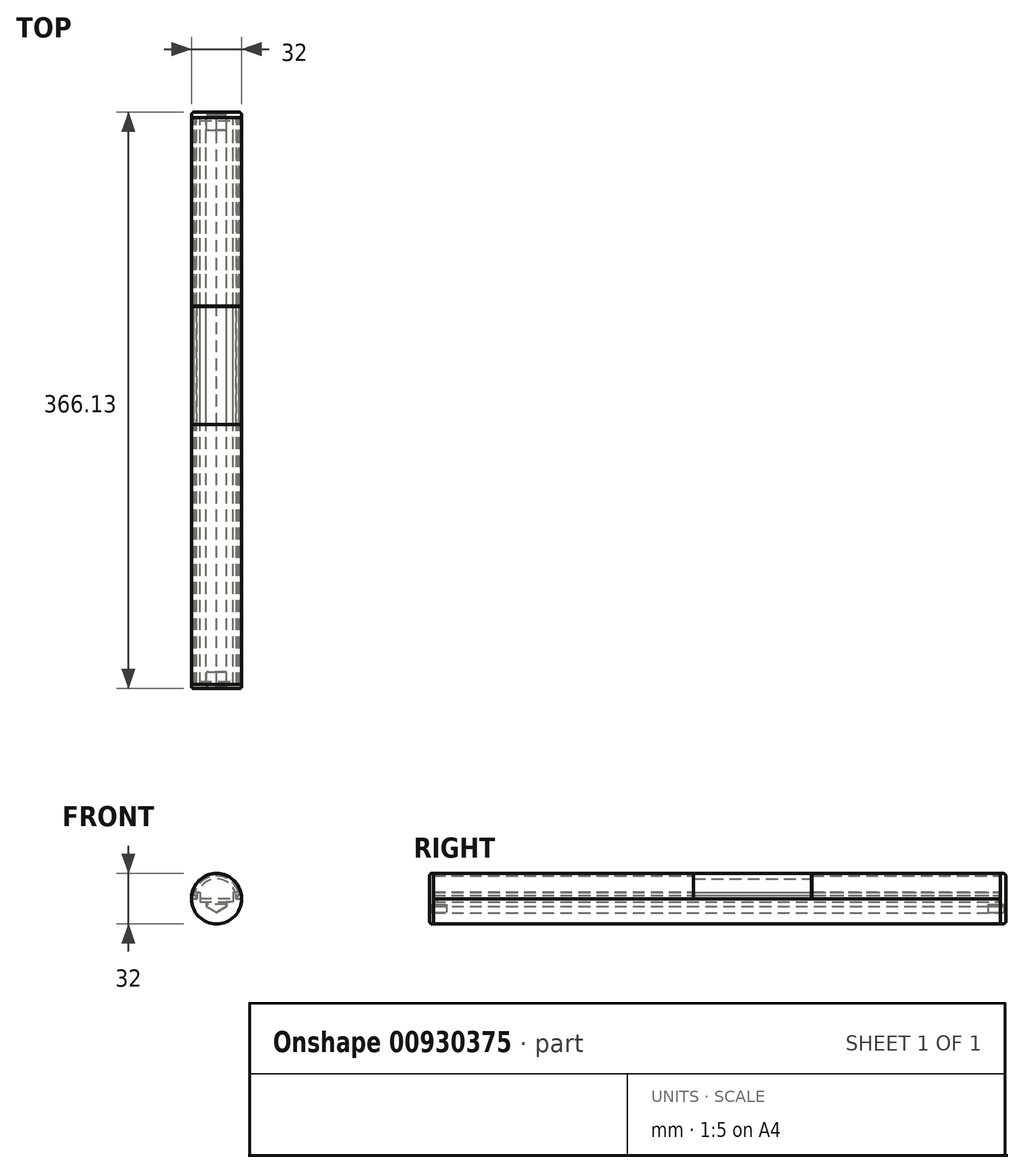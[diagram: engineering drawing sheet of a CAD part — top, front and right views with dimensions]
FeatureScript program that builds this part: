
annotation { "Feature Type Name" : "Feature", "Feature Type Description" : "" }
export const myFeature = defineFeature(function(context is Context, id is Id, definition is map)
    precondition{}
    {
        {
            var Q0;
            Q0=qCreatedBy(makeId("Front.planeOp"),FACE);
            var sketch = newSketch(context, id + "F0", { "sketchPlane" : qUnion([Q0])});
            skArc(sketch, "E0", {"start": v(0, -16) * mm, "mid": v(11.31, -11.31) * mm, "end": v(16, 0) * mm});
            skLineSegment(sketch, "E1", {"start": v(16, 0) * mm, "end": v(12.75, 0) * mm});
            skLineSegment(sketch, "E2", {"start": v(12.75, 0) * mm, "end": v(12.75, 2.1) * mm});
            skLineSegment(sketch, "E3", {"start": v(12.75, 2.1) * mm, "end": v(14.25, 2.1) * mm});
            skLineSegment(sketch, "E4", {"start": v(14.25, 2.1) * mm, "end": v(14.25, 4.1) * mm});
            skLineSegment(sketch, "E5", {"start": v(14.25, 4.1) * mm, "end": v(10.5, 4.1) * mm});
            skLineSegment(sketch, "E6", {"start": v(10.5, 4.1) * mm, "end": v(10.5, -1.9) * mm});
            skLineSegment(sketch, "E7", {"start": v(10.5, -1.9) * mm, "end": v(6.5, -1.9) * mm});
            skLineSegment(sketch, "E8", {"start": v(6.5, -1.9) * mm, "end": v(6.5, -4.9) * mm});
            skLineSegment(sketch, "E9", {"start": v(6.5, -4.9) * mm, "end": v(0, -8.88) * mm});
            skLineSegment(sketch, "E10", {"start": v(0, -8.88) * mm, "end": v(0, -16) * mm});
            skLineSegment(sketch, "E11.MirrorCS", {"start": v(-14.25, 2.1) * mm, "end": v(-14.25, 4.1) * mm});
            skLineSegment(sketch, "E12.MirrorCS", {"start": v(-12.75, 0) * mm, "end": v(-12.75, 2.1) * mm});
            skLineSegment(sketch, "E13.MirrorCS", {"start": v(-12.75, 2.1) * mm, "end": v(-14.25, 2.1) * mm});
            skLineSegment(sketch, "E14.MirrorCS", {"start": v(-6.5, -1.9) * mm, "end": v(-6.5, -4.9) * mm});
            skLineSegment(sketch, "E15.MirrorCS", {"start": v(-10.5, 4.1) * mm, "end": v(-10.5, -1.9) * mm});
            skLineSegment(sketch, "E16.MirrorCS", {"start": v(-6.5, -4.9) * mm, "end": v(0, -8.88) * mm});
            skLineSegment(sketch, "E17.MirrorCS", {"start": v(-14.25, 4.1) * mm, "end": v(-10.5, 4.1) * mm});
            skArc(sketch, "E18.MirrorCS", {"start": v(0, -16) * mm, "mid": v(-11.31, -11.31) * mm, "end": v(-16, 0) * mm});
            skLineSegment(sketch, "E19.MirrorCS", {"start": v(-10.5, -1.9) * mm, "end": v(-6.5, -1.9) * mm});
            skLineSegment(sketch, "E20.MirrorCS", {"start": v(-16, 0) * mm, "end": v(-12.75, 0) * mm});
            skSolve(sketch);
        }
        {
            var Q0;
            Q0=makeQuery(id+"F0.imprint","IMPRINT",FACE,{"disambiguationData":[TD([[makeQuery(id+"F0.imprint","IMPRINT",EDGE,{"derivedFrom":sQuery(id+"F0.wireOp",EDGE,"E0")}),1.0]])]});
            var Q1;
            Q1=makeQuery(id+"F0.imprint","IMPRINT",FACE,{"disambiguationData":[TD([[makeQuery(id+"F0.imprint","IMPRINT",EDGE,{"derivedFrom":sQuery(id+"F0.wireOp",EDGE,"E10")}),-1.0]])]});
            extrude(context, id + "F1", {"entities" : qUnion([Q0, Q1]), "endBound" : BoundingType.SYMMETRIC, "depth" : 360 * mm, "offsetDistance" : 25 * mm});
        }
        {
            var Q0;
            Q0=qCreatedBy(makeId("Front.planeOp"),FACE);
            var sketch = newSketch(context, id + "F2", { "sketchPlane" : qUnion([Q0])});
            skArc(sketch, "E21", {"start": v(16, 6.65) * mm, "mid": v(11.31, 17.96) * mm, "end": v(0, 22.65) * mm});
            skArc(sketch, "E22", {"start": v(0, 21.15) * mm, "mid": v(8.62, 18.3) * mm, "end": v(13.86, 10.9) * mm});
            skLineSegment(sketch, "E23", {"start": v(13.86, 10.9) * mm, "end": v(14.46, 10.9) * mm});
            skLineSegment(sketch, "E24", {"start": v(14.46, 10.9) * mm, "end": v(14.46, 8.65) * mm});
            skLineSegment(sketch, "E25", {"start": v(14.46, 8.65) * mm, "end": v(12.93, 8.65) * mm});
            skLineSegment(sketch, "E26", {"start": v(12.93, 8.65) * mm, "end": v(12.93, 6.65) * mm});
            skLineSegment(sketch, "E27", {"start": v(12.93, 6.65) * mm, "end": v(16, 6.65) * mm});
            skLineSegment(sketch, "E28", {"start": v(0, 22.65) * mm, "end": v(0, 21.15) * mm});
            skArc(sketch, "E29.MirrorCS", {"start": v(0, 21.15) * mm, "mid": v(-8.62, 18.3) * mm, "end": v(-13.86, 10.9) * mm});
            skArc(sketch, "E30.MirrorCS", {"start": v(-16, 6.65) * mm, "mid": v(-11.31, 17.96) * mm, "end": v(0, 22.65) * mm});
            skLineSegment(sketch, "E31.MirrorCS", {"start": v(-13.86, 10.9) * mm, "end": v(-14.46, 10.9) * mm});
            skLineSegment(sketch, "E32.MirrorCS", {"start": v(-14.46, 10.9) * mm, "end": v(-14.46, 8.65) * mm});
            skLineSegment(sketch, "E33.MirrorCS", {"start": v(-14.46, 8.65) * mm, "end": v(-12.93, 8.65) * mm});
            skLineSegment(sketch, "E34.MirrorCS", {"start": v(-12.93, 8.65) * mm, "end": v(-12.93, 6.65) * mm});
            skLineSegment(sketch, "E35.MirrorCS", {"start": v(-12.93, 6.65) * mm, "end": v(-16, 6.65) * mm});
            skSolve(sketch);
        }
        {
            var Q0;
            Q0 = qSketchRegion(id + "F2", true);
            extrude(context, id + "F3", {"entities" : qUnion([Q0]), "depth" : 120 * mm, "offsetDistance" : 25 * mm});
        }
        {
            var Q0;
            Q0=qCreatedBy(makeId("Front.planeOp"),FACE);
            var sketch = newSketch(context, id + "F4", { "sketchPlane" : qUnion([Q0])});
            skCircle(sketch, "E36", {"center": v(33.5, 0) * mm, "radius": 16 * mm});
            skSolve(sketch);
        }
        {
            var Q0;
            Q0=makeQuery(id+"F4.imprint","IMPRINT",FACE,{"disambiguationData":[TD([[makeQuery(id+"F4.imprint","IMPRINT",EDGE,{"derivedFrom":sQuery(id+"F4.wireOp",EDGE,"E36")}),1.0]])]});
            extrude(context, id + "F5", {"entities" : qUnion([Q0]), "depth" : 3.5 * mm, "offsetDistance" : 25 * mm});
        }
        {
            var Q0;
            Q0=makeQuery(id+"F3.opExtrude","SWEPT_BODY",BODY,{"disambiguationData":[OSD([sQuery(id+"F2.wireOp",EDGE,"E21"),sQuery(id+"F2.wireOp",EDGE,"E22"),sQuery(id+"F2.wireOp",EDGE,"E23"),sQuery(id+"F2.wireOp",EDGE,"E24"),sQuery(id+"F2.wireOp",EDGE,"E25"),sQuery(id+"F2.wireOp",EDGE,"E26"),sQuery(id+"F2.wireOp",EDGE,"E27"),sQuery(id+"F2.wireOp",EDGE,"E29.MirrorCS"),sQuery(id+"F2.wireOp",EDGE,"E30.MirrorCS"),sQuery(id+"F2.wireOp",EDGE,"E31.MirrorCS"),sQuery(id+"F2.wireOp",EDGE,"E32.MirrorCS"),sQuery(id+"F2.wireOp",EDGE,"E33.MirrorCS"),sQuery(id+"F2.wireOp",EDGE,"E34.MirrorCS"),sQuery(id+"F2.wireOp",EDGE,"E35.MirrorCS")])]});
            transform(context, id + "F6", {"entities" : qUnion([Q0]), "transformType" : TransformType.TRANSLATION_3D, "dx" : 0 * mm, "dy" : 155 * mm, "dz" : 0 * mm, "makeCopy" : true});
        }
        {
            var Q0;
            Q0=makeQuery(id+"F5.opExtrude","SWEPT_BODY",BODY,{"disambiguationData":[OSD([sQuery(id+"F4.wireOp",EDGE,"E36")])]});
            transform(context, id + "F7", {"entities" : qUnion([Q0]), "transformType" : TransformType.TRANSLATION_3D, "dx" : -33.5 * mm, "dy" : 184.33 * mm, "dz" : 0 * mm, "makeCopy" : false});
        }
        {
            var Q0;
            Q0=makeQuery(id+"F5.opExtrude","CAP_EDGE",EDGE,{"disambiguationData":[OSD([sQuery(id+"F4.wireOp",EDGE,"E36")])],"isStart":true});
            fillet(context, id + "F8", {"entities" : qUnion([Q0]), "radius" : 2 * mm, "tangentPropagation" : true, "allowEdgeOverflow" : false});
        }
        {
            var Q0;
            Q0=makeQuery(id+"F5.opExtrude","SWEPT_BODY",BODY,{"disambiguationData":[OSD([sQuery(id+"F4.wireOp",EDGE,"E36")])]});
            transform(context, id + "F9", {"entities" : qUnion([Q0]), "transformType" : TransformType.TRANSLATION_3D, "dx" : 0 * mm, "dy" : -0.8 * mm, "dz" : 0 * mm, "makeCopy" : false});
        }
        {
            var Q0;
            Q0=qCreatedBy(makeId("Front.planeOp"),FACE);
            var sketch = newSketch(context, id + "F10", { "sketchPlane" : qUnion([Q0])});
            skCircle(sketch, "E37", {"center": v(33.5, 0) * mm, "radius": 16 * mm});
            skSolve(sketch);
        }
        {
            var Q0;
            Q0=makeQuery(id+"F10.imprint","IMPRINT",FACE,{"disambiguationData":[TD([[makeQuery(id+"F10.imprint","IMPRINT",EDGE,{"derivedFrom":sQuery(id+"F10.wireOp",EDGE,"E37")}),1.0]])]});
            extrude(context, id + "F11", {"entities" : qUnion([Q0]), "depth" : 2.5 * mm, "offsetDistance" : 25 * mm});
        }
        {
            var Q0;
            Q0=makeQuery(id+"F11.opExtrude","SWEPT_BODY",BODY,{"disambiguationData":[OSD([sQuery(id+"F10.wireOp",EDGE,"E37")])]});
            transform(context, id + "F12", {"entities" : qUnion([Q0]), "transformType" : TransformType.TRANSLATION_3D, "dx" : 0 * mm, "dy" : -180 * mm, "dz" : 0 * mm, "makeCopy" : false});
        }
        {
            var Q0;
            Q0=makeQuery(id+"F3.opExtrude","SWEPT_BODY",BODY,{"disambiguationData":[OSD([sQuery(id+"F2.wireOp",EDGE,"E21"),sQuery(id+"F2.wireOp",EDGE,"E22"),sQuery(id+"F2.wireOp",EDGE,"E23"),sQuery(id+"F2.wireOp",EDGE,"E24"),sQuery(id+"F2.wireOp",EDGE,"E25"),sQuery(id+"F2.wireOp",EDGE,"E26"),sQuery(id+"F2.wireOp",EDGE,"E27"),sQuery(id+"F2.wireOp",EDGE,"E29.MirrorCS"),sQuery(id+"F2.wireOp",EDGE,"E30.MirrorCS"),sQuery(id+"F2.wireOp",EDGE,"E31.MirrorCS"),sQuery(id+"F2.wireOp",EDGE,"E32.MirrorCS"),sQuery(id+"F2.wireOp",EDGE,"E33.MirrorCS"),sQuery(id+"F2.wireOp",EDGE,"E34.MirrorCS"),sQuery(id+"F2.wireOp",EDGE,"E35.MirrorCS")])]});
            transform(context, id + "F13", {"entities" : qUnion([Q0]), "transformType" : TransformType.TRANSLATION_3D, "dx" : 0 * mm, "dy" : -30 * mm, "dz" : -6.7 * mm, "makeCopy" : false});
        }
        {
            var Q0;
            Q0=makeQuery(id+"F11.opExtrude","SWEPT_BODY",BODY,{"disambiguationData":[OSD([sQuery(id+"F10.wireOp",EDGE,"E37")])]});
            transform(context, id + "F14", {"entities" : qUnion([Q0]), "transformType" : TransformType.TRANSLATION_3D, "dx" : -33.5 * mm, "dy" : 0 * mm, "dz" : 0 * mm, "makeCopy" : false});
        }
        {
            var Q0;
            Q0=makeQuery(id+"F11.opExtrude","CAP_EDGE",EDGE,{"disambiguationData":[OSD([sQuery(id+"F10.wireOp",EDGE,"E37")])],"isStart":false});
            fillet(context, id + "F15", {"entities" : qUnion([Q0]), "radius" : 1.5 * mm, "tangentPropagation" : true, "allowEdgeOverflow" : false});
        }
        {
            var Q0;
            Q0=makeQuery(id+"F3.opExtrude","SWEPT_BODY",BODY,{"disambiguationData":[OSD([sQuery(id+"F2.wireOp",EDGE,"E21"),sQuery(id+"F2.wireOp",EDGE,"E22"),sQuery(id+"F2.wireOp",EDGE,"E23"),sQuery(id+"F2.wireOp",EDGE,"E24"),sQuery(id+"F2.wireOp",EDGE,"E25"),sQuery(id+"F2.wireOp",EDGE,"E26"),sQuery(id+"F2.wireOp",EDGE,"E27"),sQuery(id+"F2.wireOp",EDGE,"E29.MirrorCS"),sQuery(id+"F2.wireOp",EDGE,"E30.MirrorCS"),sQuery(id+"F2.wireOp",EDGE,"E31.MirrorCS"),sQuery(id+"F2.wireOp",EDGE,"E32.MirrorCS"),sQuery(id+"F2.wireOp",EDGE,"E33.MirrorCS"),sQuery(id+"F2.wireOp",EDGE,"E34.MirrorCS"),sQuery(id+"F2.wireOp",EDGE,"E35.MirrorCS")])]});
            transform(context, id + "F16", {"entities" : qUnion([Q0]), "transformType" : TransformType.TRANSLATION_3D, "dx" : 0 * mm, "dy" : 210.3 * mm, "dz" : 0 * mm, "makeCopy" : true});
        }
        {
            var Q0;
            Q0=makeQuery(id+"F6.opPattern","COPY",BODY,{"derivedFrom":makeQuery(id+"F3.opExtrude","SWEPT_BODY",BODY,{"disambiguationData":[OSD([sQuery(id+"F2.wireOp",EDGE,"E21"),sQuery(id+"F2.wireOp",EDGE,"E22"),sQuery(id+"F2.wireOp",EDGE,"E23"),sQuery(id+"F2.wireOp",EDGE,"E24"),sQuery(id+"F2.wireOp",EDGE,"E25"),sQuery(id+"F2.wireOp",EDGE,"E26"),sQuery(id+"F2.wireOp",EDGE,"E27"),sQuery(id+"F2.wireOp",EDGE,"E29.MirrorCS"),sQuery(id+"F2.wireOp",EDGE,"E30.MirrorCS"),sQuery(id+"F2.wireOp",EDGE,"E31.MirrorCS"),sQuery(id+"F2.wireOp",EDGE,"E32.MirrorCS"),sQuery(id+"F2.wireOp",EDGE,"E33.MirrorCS"),sQuery(id+"F2.wireOp",EDGE,"E34.MirrorCS"),sQuery(id+"F2.wireOp",EDGE,"E35.MirrorCS")])]}),"instanceName":"1"});
            deleteBodies(context, id + "F17", {"entities" : qUnion([Q0])});
        }
        {
            var Q0;
            Q0=qCreatedBy(makeId("Front.planeOp"),FACE);
            var sketch = newSketch(context, id + "F18", { "sketchPlane" : qUnion([Q0])});
            skArc(sketch, "E38", {"start": v(0, 44) * mm, "mid": v(11.31, 39.31) * mm, "end": v(16, 28) * mm});
            skArc(sketch, "E39", {"start": v(0, 42.5) * mm, "mid": v(8.64, 39.64) * mm, "end": v(13.88, 32.2) * mm});
            skLineSegment(sketch, "E40", {"start": v(13.88, 32.2) * mm, "end": v(14.48, 32.2) * mm});
            skLineSegment(sketch, "E41", {"start": v(14.48, 32.2) * mm, "end": v(14.49, 29.95) * mm});
            skLineSegment(sketch, "E42", {"start": v(14.49, 29.95) * mm, "end": v(12.99, 29.95) * mm});
            skLineSegment(sketch, "E43", {"start": v(12.99, 29.95) * mm, "end": v(13, 27.95) * mm});
            skLineSegment(sketch, "E44", {"start": v(13, 27.95) * mm, "end": v(16, 28) * mm});
            skLineSegment(sketch, "E45", {"start": v(0, 44) * mm, "end": v(0, 42.5) * mm});
            skArc(sketch, "E46.MirrorCS", {"start": v(0, 44) * mm, "mid": v(-11.31, 39.31) * mm, "end": v(-16, 28) * mm});
            skArc(sketch, "E47.MirrorCS", {"start": v(0, 42.5) * mm, "mid": v(-8.64, 39.64) * mm, "end": v(-13.88, 32.2) * mm});
            skLineSegment(sketch, "E48.MirrorCS", {"start": v(-13.88, 32.2) * mm, "end": v(-14.48, 32.2) * mm});
            skLineSegment(sketch, "E49.MirrorCS", {"start": v(-14.48, 32.2) * mm, "end": v(-14.49, 29.95) * mm});
            skLineSegment(sketch, "E50.MirrorCS", {"start": v(-14.49, 29.95) * mm, "end": v(-12.99, 29.95) * mm});
            skLineSegment(sketch, "E51.MirrorCS", {"start": v(-12.99, 29.95) * mm, "end": v(-13, 27.95) * mm});
            skLineSegment(sketch, "E52.MirrorCS", {"start": v(-13, 27.95) * mm, "end": v(-16, 28) * mm});
            skSolve(sketch);
        }
        {
            var Q0;
            Q0 = qSketchRegion(id + "F18", true);
            extrude(context, id + "F19", {"entities" : qUnion([Q0]), "endBound" : BoundingType.SYMMETRIC, "depth" : 165 * mm, "offsetDistance" : 25 * mm});
        }
        {
            var Q0;
            Q0=makeQuery(id+"F19.opExtrude","SWEPT_BODY",BODY,{"disambiguationData":[OSD([sQuery(id+"F18.wireOp",EDGE,"E38"),sQuery(id+"F18.wireOp",EDGE,"E39"),sQuery(id+"F18.wireOp",EDGE,"E40"),sQuery(id+"F18.wireOp",EDGE,"E41"),sQuery(id+"F18.wireOp",EDGE,"E42"),sQuery(id+"F18.wireOp",EDGE,"E43"),sQuery(id+"F18.wireOp",EDGE,"E44"),sQuery(id+"F18.wireOp",EDGE,"E46.MirrorCS"),sQuery(id+"F18.wireOp",EDGE,"E47.MirrorCS"),sQuery(id+"F18.wireOp",EDGE,"E48.MirrorCS"),sQuery(id+"F18.wireOp",EDGE,"E49.MirrorCS"),sQuery(id+"F18.wireOp",EDGE,"E50.MirrorCS"),sQuery(id+"F18.wireOp",EDGE,"E51.MirrorCS"),sQuery(id+"F18.wireOp",EDGE,"E52.MirrorCS")])]});
            transform(context, id + "F20", {"entities" : qUnion([Q0]), "transformType" : TransformType.TRANSLATION_3D, "dx" : 0 * mm, "dy" : 90 * mm, "dz" : -28 * mm, "makeCopy" : false});
        }
        {
            var Q0;
            Q0=makeQuery(id+"F3.opExtrude","SWEPT_BODY",BODY,{"disambiguationData":[OSD([sQuery(id+"F2.wireOp",EDGE,"E21"),sQuery(id+"F2.wireOp",EDGE,"E22"),sQuery(id+"F2.wireOp",EDGE,"E23"),sQuery(id+"F2.wireOp",EDGE,"E24"),sQuery(id+"F2.wireOp",EDGE,"E25"),sQuery(id+"F2.wireOp",EDGE,"E26"),sQuery(id+"F2.wireOp",EDGE,"E27"),sQuery(id+"F2.wireOp",EDGE,"E29.MirrorCS"),sQuery(id+"F2.wireOp",EDGE,"E30.MirrorCS"),sQuery(id+"F2.wireOp",EDGE,"E31.MirrorCS"),sQuery(id+"F2.wireOp",EDGE,"E32.MirrorCS"),sQuery(id+"F2.wireOp",EDGE,"E33.MirrorCS"),sQuery(id+"F2.wireOp",EDGE,"E34.MirrorCS"),sQuery(id+"F2.wireOp",EDGE,"E35.MirrorCS")])]});
            deleteBodies(context, id + "F21", {"entities" : qUnion([Q0])});
        }
        {
            var Q0;
            Q0=makeQuery(id+"F19.opExtrude","SWEPT_BODY",BODY,{"disambiguationData":[OSD([sQuery(id+"F18.wireOp",EDGE,"E38"),sQuery(id+"F18.wireOp",EDGE,"E39"),sQuery(id+"F18.wireOp",EDGE,"E40"),sQuery(id+"F18.wireOp",EDGE,"E41"),sQuery(id+"F18.wireOp",EDGE,"E42"),sQuery(id+"F18.wireOp",EDGE,"E43"),sQuery(id+"F18.wireOp",EDGE,"E44"),sQuery(id+"F18.wireOp",EDGE,"E46.MirrorCS"),sQuery(id+"F18.wireOp",EDGE,"E47.MirrorCS"),sQuery(id+"F18.wireOp",EDGE,"E48.MirrorCS"),sQuery(id+"F18.wireOp",EDGE,"E49.MirrorCS"),sQuery(id+"F18.wireOp",EDGE,"E50.MirrorCS"),sQuery(id+"F18.wireOp",EDGE,"E51.MirrorCS"),sQuery(id+"F18.wireOp",EDGE,"E52.MirrorCS")])]});
            transform(context, id + "F22", {"entities" : qUnion([Q0]), "transformType" : TransformType.TRANSLATION_3D, "dx" : 0 * mm, "dy" : -149.5 * mm, "dz" : 0 * mm, "makeCopy" : false});
        }
        {
            var Q0;
            Q0=makeQuery(id+"F11.opExtrude","SWEPT_BODY",BODY,{"disambiguationData":[OSD([sQuery(id+"F10.wireOp",EDGE,"E37")])]});
            transform(context, id + "F23", {"entities" : qUnion([Q0]), "transformType" : TransformType.TRANSLATION_3D, "dx" : 0 * mm, "dy" : -45.1 * mm, "dz" : 0 * mm, "makeCopy" : false});
        }
        {
            var Q0;
            Q0=makeQuery(id+"F19.opExtrude","SWEPT_BODY",BODY,{"disambiguationData":[OSD([sQuery(id+"F18.wireOp",EDGE,"E38"),sQuery(id+"F18.wireOp",EDGE,"E39"),sQuery(id+"F18.wireOp",EDGE,"E40"),sQuery(id+"F18.wireOp",EDGE,"E41"),sQuery(id+"F18.wireOp",EDGE,"E42"),sQuery(id+"F18.wireOp",EDGE,"E43"),sQuery(id+"F18.wireOp",EDGE,"E44"),sQuery(id+"F18.wireOp",EDGE,"E46.MirrorCS"),sQuery(id+"F18.wireOp",EDGE,"E47.MirrorCS"),sQuery(id+"F18.wireOp",EDGE,"E48.MirrorCS"),sQuery(id+"F18.wireOp",EDGE,"E49.MirrorCS"),sQuery(id+"F18.wireOp",EDGE,"E50.MirrorCS"),sQuery(id+"F18.wireOp",EDGE,"E51.MirrorCS"),sQuery(id+"F18.wireOp",EDGE,"E52.MirrorCS")])]});
            transform(context, id + "F24", {"entities" : qUnion([Q0]), "transformType" : TransformType.TRANSLATION_3D, "dx" : 0 * mm, "dy" : -45.55 * mm, "dz" : 0 * mm, "makeCopy" : false});
        }
        {
            var Q0;
            Q0=qCreatedBy(makeId("Front.planeOp"),FACE);
            var sketch = newSketch(context, id + "F25", { "sketchPlane" : qUnion([Q0])});
            skLineSegment(sketch, "E53", {"start": v(-6.4, -4.8) * mm, "end": v(0, -8.7) * mm});
            skLineSegment(sketch, "E54", {"start": v(0, -8.7) * mm, "end": v(6.4, -4.8) * mm});
            skLineSegment(sketch, "E55", {"start": v(6.4, -4.8) * mm, "end": v(6.4, -3.55) * mm});
            skLineSegment(sketch, "E56", {"start": v(6.4, -3.55) * mm, "end": v(-6.4, -3.55) * mm});
            skLineSegment(sketch, "E57", {"start": v(-6.4, -3.55) * mm, "end": v(-6.4, -4.8) * mm});
            skSolve(sketch);
        }
        {
            var Q0;
            Q0=makeQuery(id+"F25.imprint","IMPRINT",FACE,{"disambiguationData":[TD([[makeQuery(id+"F25.imprint","IMPRINT",EDGE,{"derivedFrom":sQuery(id+"F25.wireOp",EDGE,"E53")}),1.0]])]});
            extrude(context, id + "F26", {"entities" : qUnion([Q0]), "depth" : 10 * mm, "offsetDistance" : 25 * mm});
        }
        {
            var Q0;
            Q0=makeQuery(id+"F26.opExtrude","SWEPT_BODY",BODY,{"disambiguationData":[OSD([sQuery(id+"F25.wireOp",EDGE,"E53"),sQuery(id+"F25.wireOp",EDGE,"E54"),sQuery(id+"F25.wireOp",EDGE,"E55"),sQuery(id+"F25.wireOp",EDGE,"E56"),sQuery(id+"F25.wireOp",EDGE,"E57")])]});
            transform(context, id + "F27", {"entities" : qUnion([Q0]), "transformType" : TransformType.TRANSLATION_3D, "dx" : 0 * mm, "dy" : -172 * mm, "dz" : 0 * mm, "makeCopy" : false});
        }
        {
            var Q0;
            Q0=makeQuery(id+"F26.opExtrude","SWEPT_BODY",BODY,{"disambiguationData":[OSD([sQuery(id+"F25.wireOp",EDGE,"E53"),sQuery(id+"F25.wireOp",EDGE,"E54"),sQuery(id+"F25.wireOp",EDGE,"E55"),sQuery(id+"F25.wireOp",EDGE,"E56"),sQuery(id+"F25.wireOp",EDGE,"E57")])]});
            transform(context, id + "F28", {"entities" : qUnion([Q0]), "transformType" : TransformType.TRANSLATION_3D, "dx" : 0 * mm, "dy" : 354 * mm, "dz" : 0 * mm, "makeCopy" : true});
        }
        {
            var Q0;
            Q0=qCreatedBy(makeId("Front.planeOp"),FACE);
            var sketch = newSketch(context, id + "F29", { "sketchPlane" : qUnion([Q0])});
            skArc(sketch, "E58", {"start": v(16, 12) * mm, "mid": v(0, 28) * mm, "end": v(-16, 12) * mm});
            skArc(sketch, "E59", {"start": v(-12.5, 12) * mm, "mid": v(0, 24.5) * mm, "end": v(12.5, 12) * mm});
            skLineSegment(sketch, "E60", {"start": v(-16, 12) * mm, "end": v(-12.5, 12) * mm});
            skLineSegment(sketch, "E61", {"start": v(12.5, 12) * mm, "end": v(16, 12) * mm});
            skSolve(sketch);
        }
        {
            var Q0;
            Q0 = qSketchRegion(id + "F29", true);
            extrude(context, id + "F30", {"entities" : qUnion([Q0]), "depth" : 75 * mm, "offsetDistance" : 25 * mm});
        }
        {
            var Q0;
            Q0=makeQuery(id+"F30.opExtrude","SWEPT_BODY",BODY,{"disambiguationData":[OSD([sQuery(id+"F29.wireOp",EDGE,"E58"),sQuery(id+"F29.wireOp",EDGE,"E59"),sQuery(id+"F29.wireOp",EDGE,"E60"),sQuery(id+"F29.wireOp",EDGE,"E61")])]});
            transform(context, id + "F31", {"entities" : qUnion([Q0]), "transformType" : TransformType.TRANSLATION_3D, "dx" : 0 * mm, "dy" : 15 * mm, "dz" : -12 * mm, "makeCopy" : false});
        }
        {
            var Q0;
            Q0=makeQuery(id+"F19.opExtrude","SWEPT_BODY",BODY,{"disambiguationData":[OSD([sQuery(id+"F18.wireOp",EDGE,"E38"),sQuery(id+"F18.wireOp",EDGE,"E39"),sQuery(id+"F18.wireOp",EDGE,"E40"),sQuery(id+"F18.wireOp",EDGE,"E41"),sQuery(id+"F18.wireOp",EDGE,"E42"),sQuery(id+"F18.wireOp",EDGE,"E43"),sQuery(id+"F18.wireOp",EDGE,"E44"),sQuery(id+"F18.wireOp",EDGE,"E46.MirrorCS"),sQuery(id+"F18.wireOp",EDGE,"E47.MirrorCS"),sQuery(id+"F18.wireOp",EDGE,"E48.MirrorCS"),sQuery(id+"F18.wireOp",EDGE,"E49.MirrorCS"),sQuery(id+"F18.wireOp",EDGE,"E50.MirrorCS"),sQuery(id+"F18.wireOp",EDGE,"E51.MirrorCS"),sQuery(id+"F18.wireOp",EDGE,"E52.MirrorCS")])]});
            transform(context, id + "F32", {"entities" : qUnion([Q0]), "transformType" : TransformType.TRANSLATION_3D, "dx" : 0 * mm, "dy" : -15 * mm, "dz" : 0 * mm, "makeCopy" : false});
        }
        {
            var Q0;
            Q0=makeQuery(id+"F30.opExtrude","SWEPT_BODY",BODY,{"disambiguationData":[OSD([sQuery(id+"F29.wireOp",EDGE,"E58"),sQuery(id+"F29.wireOp",EDGE,"E59"),sQuery(id+"F29.wireOp",EDGE,"E60"),sQuery(id+"F29.wireOp",EDGE,"E61")])]});
            transform(context, id + "F33", {"entities" : qUnion([Q0]), "transformType" : TransformType.TRANSLATION_3D, "dx" : 0 * mm, "dy" : 45 * mm, "dz" : 0 * mm, "makeCopy" : false});
        }
        {
            var Q0;
            Q0=makeQuery(id+"F19.opExtrude","SWEPT_BODY",BODY,{"disambiguationData":[OSD([sQuery(id+"F18.wireOp",EDGE,"E38"),sQuery(id+"F18.wireOp",EDGE,"E39"),sQuery(id+"F18.wireOp",EDGE,"E40"),sQuery(id+"F18.wireOp",EDGE,"E41"),sQuery(id+"F18.wireOp",EDGE,"E42"),sQuery(id+"F18.wireOp",EDGE,"E43"),sQuery(id+"F18.wireOp",EDGE,"E44"),sQuery(id+"F18.wireOp",EDGE,"E46.MirrorCS"),sQuery(id+"F18.wireOp",EDGE,"E47.MirrorCS"),sQuery(id+"F18.wireOp",EDGE,"E48.MirrorCS"),sQuery(id+"F18.wireOp",EDGE,"E49.MirrorCS"),sQuery(id+"F18.wireOp",EDGE,"E50.MirrorCS"),sQuery(id+"F18.wireOp",EDGE,"E51.MirrorCS"),sQuery(id+"F18.wireOp",EDGE,"E52.MirrorCS")])]});
            transform(context, id + "F34", {"entities" : qUnion([Q0]), "transformType" : TransformType.TRANSLATION_3D, "dx" : 0 * mm, "dy" : 45 * mm, "dz" : 0 * mm, "makeCopy" : false});
        }
        {
            var Q0;
            Q0=makeQuery(id+"F19.opExtrude","SWEPT_BODY",BODY,{"disambiguationData":[OSD([sQuery(id+"F18.wireOp",EDGE,"E38"),sQuery(id+"F18.wireOp",EDGE,"E39"),sQuery(id+"F18.wireOp",EDGE,"E40"),sQuery(id+"F18.wireOp",EDGE,"E41"),sQuery(id+"F18.wireOp",EDGE,"E42"),sQuery(id+"F18.wireOp",EDGE,"E43"),sQuery(id+"F18.wireOp",EDGE,"E44"),sQuery(id+"F18.wireOp",EDGE,"E46.MirrorCS"),sQuery(id+"F18.wireOp",EDGE,"E47.MirrorCS"),sQuery(id+"F18.wireOp",EDGE,"E48.MirrorCS"),sQuery(id+"F18.wireOp",EDGE,"E49.MirrorCS"),sQuery(id+"F18.wireOp",EDGE,"E50.MirrorCS"),sQuery(id+"F18.wireOp",EDGE,"E51.MirrorCS"),sQuery(id+"F18.wireOp",EDGE,"E52.MirrorCS")])]});
            transform(context, id + "F35", {"entities" : qUnion([Q0]), "transformType" : TransformType.TRANSLATION_3D, "dx" : 0 * mm, "dy" : -22.5 * mm, "dz" : 0 * mm, "makeCopy" : false});
        }
        {
            var Q0;
            Q0=qCreatedBy(makeId("Front.planeOp"),FACE);
            var sketch = newSketch(context, id + "F36", { "sketchPlane" : qUnion([Q0])});
            skLineSegment(sketch, "E62.bottom", {"start": v(-10.55, 10) * mm, "end": v(10.45, 10) * mm});
            skLineSegment(sketch, "E62.top", {"start": v(-10.55, 8) * mm, "end": v(10.45, 8) * mm});
            skLineSegment(sketch, "E62.left", {"start": v(-10.55, 10) * mm, "end": v(-10.55, 8) * mm});
            skLineSegment(sketch, "E62.right", {"start": v(10.45, 10) * mm, "end": v(10.45, 8) * mm});
            skSolve(sketch);
        }
        {
            var Q0;
            Q0 = qSketchRegion(id + "F36", true);
            extrude(context, id + "F37", {"entities" : qUnion([Q0]), "depth" : 2 * mm, "offsetDistance" : 25 * mm});
        }
        {
            var Q0;
            Q0=makeQuery(id+"F37.opExtrude","SWEPT_BODY",BODY,{"disambiguationData":[OSD([sQuery(id+"F36.wireOp",EDGE,"E62.bottom"),sQuery(id+"F36.wireOp",EDGE,"E62.top"),sQuery(id+"F36.wireOp",EDGE,"E62.left"),sQuery(id+"F36.wireOp",EDGE,"E62.right")])]});
            transform(context, id + "F38", {"entities" : qUnion([Q0]), "transformType" : TransformType.TRANSLATION_3D, "dx" : 0 * mm, "dy" : -178 * mm, "dz" : -9.9 * mm, "makeCopy" : false});
        }
        {
            var Q0;
            Q0=makeQuery(id+"F37.opExtrude","SWEPT_BODY",BODY,{"disambiguationData":[OSD([sQuery(id+"F36.wireOp",EDGE,"E62.bottom"),sQuery(id+"F36.wireOp",EDGE,"E62.top"),sQuery(id+"F36.wireOp",EDGE,"E62.left"),sQuery(id+"F36.wireOp",EDGE,"E62.right")])]});
            transform(context, id + "F39", {"entities" : qUnion([Q0]), "transformType" : TransformType.TRANSLATION_3D, "dx" : 0 * mm, "dy" : 358 * mm, "dz" : 0 * mm, "makeCopy" : true});
        }
        {
            var Q0;
            Q0=makeQuery(id+"F11.opExtrude","SWEPT_BODY",BODY,{"disambiguationData":[OSD([sQuery(id+"F10.wireOp",EDGE,"E37")])]});
            transform(context, id + "F40", {"entities" : qUnion([Q0]), "transformType" : TransformType.TRANSLATION_3D, "dx" : 0 * mm, "dy" : 45 * mm, "dz" : 0 * mm, "makeCopy" : false});
        }
    });
